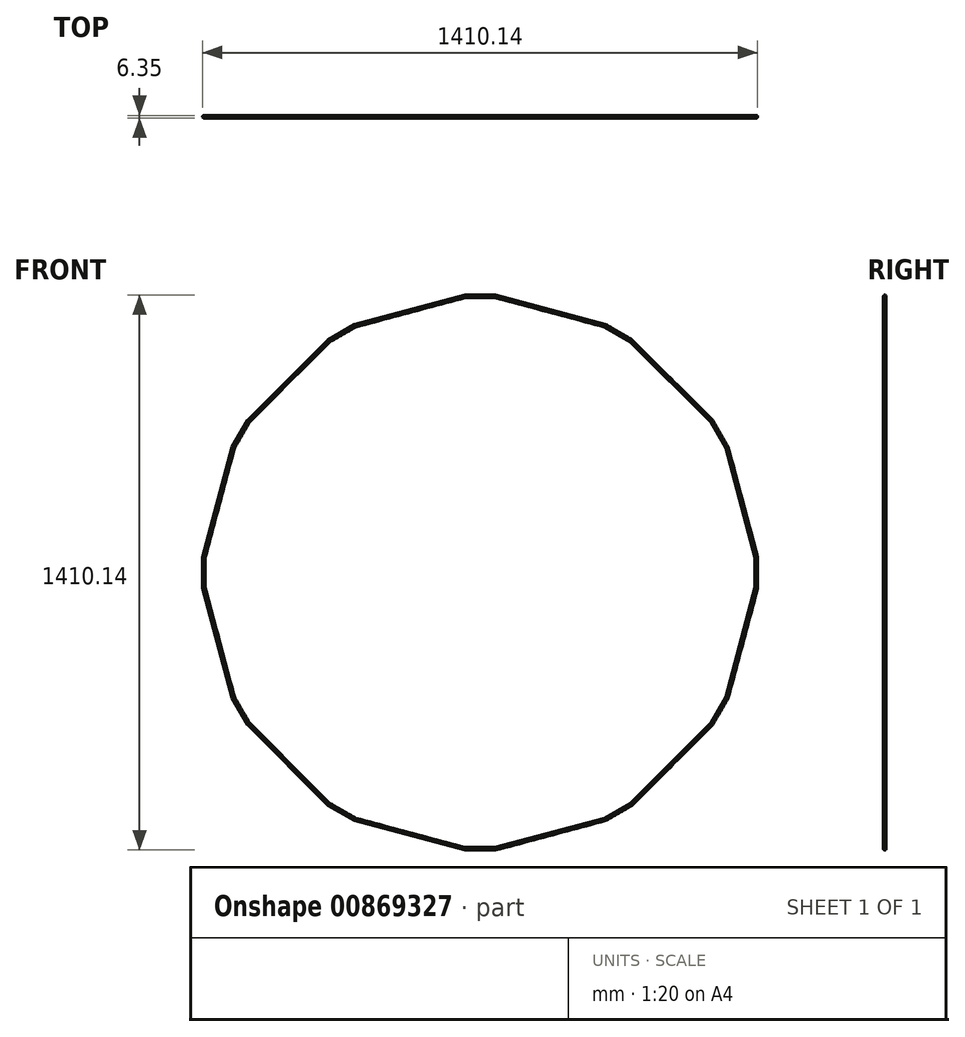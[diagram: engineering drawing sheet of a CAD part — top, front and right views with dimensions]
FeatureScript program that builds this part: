
annotation { "Feature Type Name" : "Feature", "Feature Type Description" : "" }
export const myFeature = defineFeature(function(context is Context, id is Id, definition is map)
    precondition{}
    {
        {
            var Q0;
            Q0=qCreatedBy(makeId("Front.planeOp"),FACE);
            var sketch = newSketch(context, id + "F0", { "sketchPlane" : qUnion([Q0])});
            skLineSegment(sketch, "E0", {"start": v(-38.1, 698.88) * mm, "end": v(38.1, 698.88) * mm});
            skLineSegment(sketch, "E1", {"start": v(38.1, 698.88) * mm, "end": v(316.44, 624.3) * mm});
            skLineSegment(sketch, "E2", {"start": v(316.44, 624.3) * mm, "end": v(382.44, 586.2) * mm});
            skLineSegment(sketch, "E3", {"start": v(382.44, 586.2) * mm, "end": v(586.2, 382.44) * mm});
            skLineSegment(sketch, "E4", {"start": v(586.2, 382.44) * mm, "end": v(624.3, 316.44) * mm});
            skLineSegment(sketch, "E5", {"start": v(624.3, 316.44) * mm, "end": v(698.88, 38.1) * mm});
            skLineSegment(sketch, "E6", {"start": v(698.88, 38.1) * mm, "end": v(698.88, -38.1) * mm});
            skLineSegment(sketch, "E7", {"start": v(698.88, -38.1) * mm, "end": v(624.3, -316.44) * mm});
            skLineSegment(sketch, "E8", {"start": v(624.3, -316.44) * mm, "end": v(586.2, -382.44) * mm});
            skLineSegment(sketch, "E9", {"start": v(586.2, -382.44) * mm, "end": v(382.44, -586.2) * mm});
            skLineSegment(sketch, "E10", {"start": v(382.44, -586.2) * mm, "end": v(316.44, -624.3) * mm});
            skLineSegment(sketch, "E11", {"start": v(316.44, -624.3) * mm, "end": v(38.1, -698.88) * mm});
            skLineSegment(sketch, "E12", {"start": v(38.1, -698.88) * mm, "end": v(-38.1, -698.88) * mm});
            skLineSegment(sketch, "E13", {"start": v(-38.1, -698.88) * mm, "end": v(-316.44, -624.3) * mm});
            skLineSegment(sketch, "E14", {"start": v(-316.44, -624.3) * mm, "end": v(-382.44, -586.2) * mm});
            skLineSegment(sketch, "E15", {"start": v(-382.44, -586.2) * mm, "end": v(-586.2, -382.44) * mm});
            skLineSegment(sketch, "E16", {"start": v(-586.2, -382.44) * mm, "end": v(-624.3, -316.44) * mm});
            skLineSegment(sketch, "E17", {"start": v(-624.3, -316.44) * mm, "end": v(-698.88, -38.1) * mm});
            skLineSegment(sketch, "E18", {"start": v(-698.88, -38.1) * mm, "end": v(-698.88, 38.1) * mm});
            skLineSegment(sketch, "E19", {"start": v(-698.88, 38.1) * mm, "end": v(-624.3, 316.44) * mm});
            skLineSegment(sketch, "E20", {"start": v(-624.3, 316.44) * mm, "end": v(-586.2, 382.44) * mm});
            skLineSegment(sketch, "E21", {"start": v(-586.2, 382.44) * mm, "end": v(-382.44, 586.2) * mm});
            skLineSegment(sketch, "E22", {"start": v(-382.44, 586.2) * mm, "end": v(-316.44, 624.3) * mm});
            skLineSegment(sketch, "E23", {"start": v(-316.44, 624.3) * mm, "end": v(-38.1, 698.88) * mm});
            skSolve(sketch);
        }
        {
            var Q0;
            Q0=qCreatedBy(makeId("Right.planeOp"),FACE);
            var sketch = newSketch(context, id + "F1", { "sketchPlane" : qUnion([Q0])});
            skCircle(sketch, "E24", {"center": v(0.98, 701.9) * mm, "radius": 3.18 * mm});
            skSolve(sketch);
        }
        {
            var Q0;
            Q0=makeQuery(id+"F1.imprint","IMPRINT",FACE,{"disambiguationData":[TD([[makeQuery(id+"F1.imprint","IMPRINT",EDGE,{"derivedFrom":sQuery(id+"F1.wireOp",EDGE,"E24")}),1.0]])]});
            var Q1;
            Q1=sQuery(id+"F0.wireOp",EDGE,"E0");
            var Q2;
            Q2=sQuery(id+"F0.wireOp",EDGE,"E1");
            var Q3;
            Q3=sQuery(id+"F0.wireOp",EDGE,"E2");
            var Q4;
            Q4=sQuery(id+"F0.wireOp",EDGE,"E3");
            var Q5;
            Q5=sQuery(id+"F0.wireOp",EDGE,"E4");
            var Q6;
            Q6=sQuery(id+"F0.wireOp",EDGE,"E5");
            var Q7;
            Q7=sQuery(id+"F0.wireOp",EDGE,"E6");
            var Q8;
            Q8=sQuery(id+"F0.wireOp",EDGE,"E7");
            var Q9;
            Q9=sQuery(id+"F0.wireOp",EDGE,"E8");
            var Q10;
            Q10=sQuery(id+"F0.wireOp",EDGE,"E9");
            var Q11;
            Q11=sQuery(id+"F0.wireOp",EDGE,"E10");
            var Q12;
            Q12=sQuery(id+"F0.wireOp",EDGE,"E11");
            var Q13;
            Q13=sQuery(id+"F0.wireOp",EDGE,"E12");
            var Q14;
            Q14=sQuery(id+"F0.wireOp",EDGE,"E13");
            var Q15;
            Q15=sQuery(id+"F0.wireOp",EDGE,"E14");
            var Q16;
            Q16=sQuery(id+"F0.wireOp",EDGE,"E15");
            var Q17;
            Q17=sQuery(id+"F0.wireOp",EDGE,"E16");
            var Q18;
            Q18=sQuery(id+"F0.wireOp",EDGE,"E17");
            var Q19;
            Q19=sQuery(id+"F0.wireOp",EDGE,"E18");
            var Q20;
            Q20=sQuery(id+"F0.wireOp",EDGE,"E19");
            var Q21;
            Q21=sQuery(id+"F0.wireOp",EDGE,"E20");
            var Q22;
            Q22=sQuery(id+"F0.wireOp",EDGE,"E21");
            var Q23;
            Q23=sQuery(id+"F0.wireOp",EDGE,"E22");
            var Q24;
            Q24=sQuery(id+"F0.wireOp",EDGE,"E23");
            sweep(context, id + "F2", {"profiles" : qUnion([Q0]), "path" : qUnion([Q1, Q2, Q3, Q4, Q5, Q6, Q7, Q8, Q9, Q10, Q11, Q12, Q13, Q14, Q15, Q16, Q17, Q18, Q19, Q20, Q21, Q22, Q23, Q24])});
        }
    });
